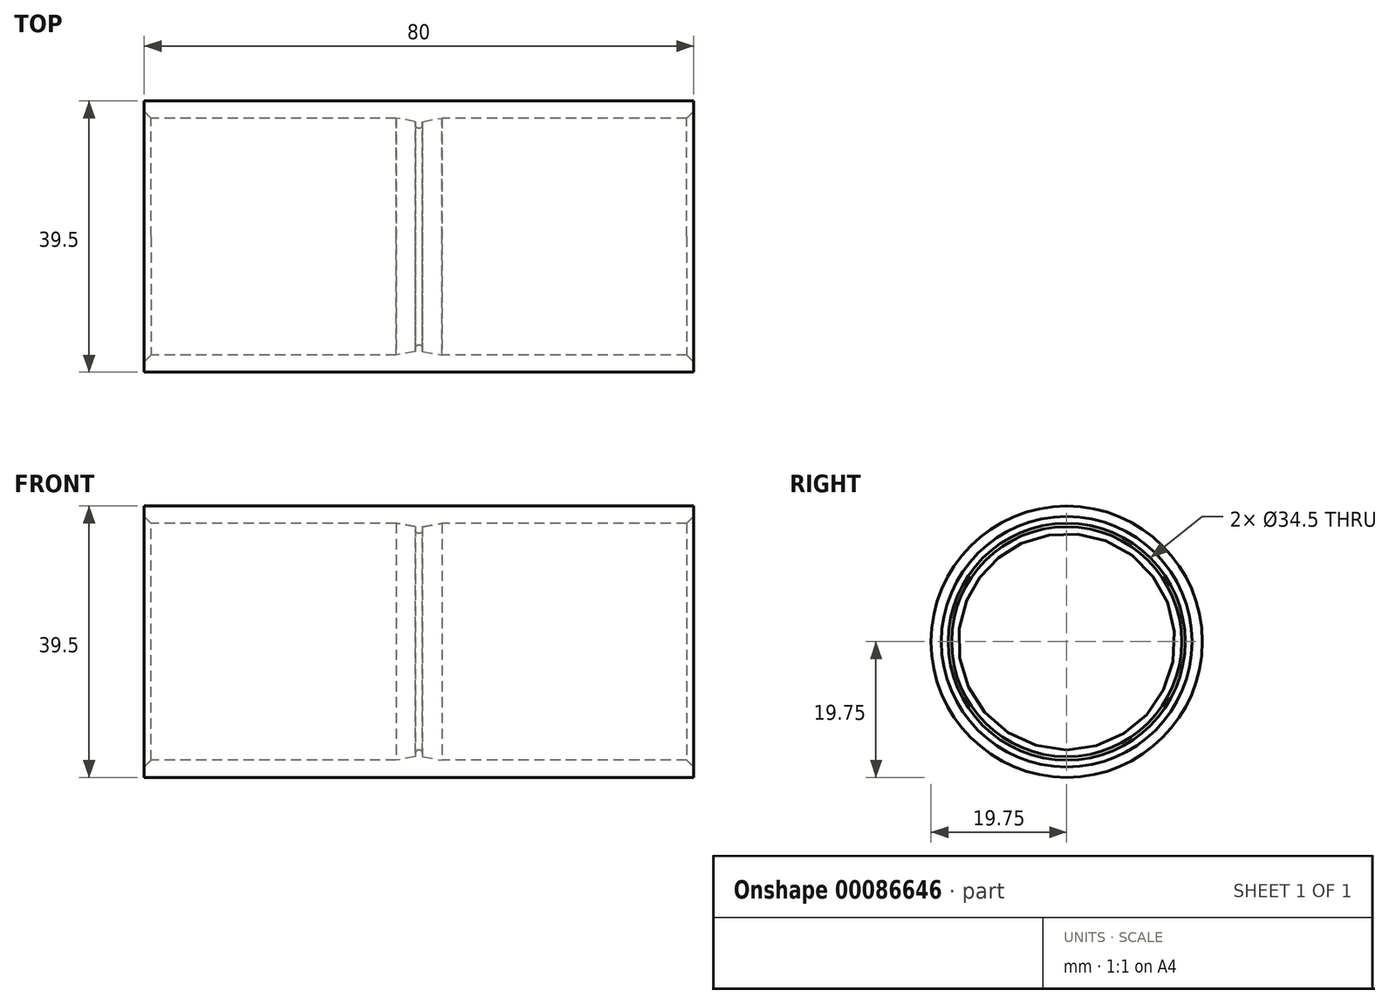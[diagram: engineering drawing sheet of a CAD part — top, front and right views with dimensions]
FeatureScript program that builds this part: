
annotation { "Feature Type Name" : "Feature", "Feature Type Description" : "" }
export const myFeature = defineFeature(function(context is Context, id is Id, definition is map)
    precondition{}
    {
        {
            var Q0;
            Q0=qCreatedBy(makeId("Top.planeOp"),FACE);
            var sketch = newSketch(context, id + "F0", { "sketchPlane" : qUnion([Q0])});
            skLineSegment(sketch, "E0", {"start": v(-40, 0) * mm, "end": v(40, 0) * mm, "construction": true});
            skLineSegment(sketch, "E1", {"start": v(-40, 19.75) * mm, "end": v(-40, 17.25) * mm});
            skLineSegment(sketch, "E2", {"start": v(-40, 17.25) * mm, "end": v(-3.34, 17.25) * mm});
            skLineSegment(sketch, "E3", {"start": v(-3.34, 17.25) * mm, "end": v(-0.5, 16.75) * mm});
            skLineSegment(sketch, "E4", {"start": v(-0.5, 16.75) * mm, "end": v(-0.5, 15.75) * mm});
            skLineSegment(sketch, "E5", {"start": v(0, 0) * mm, "end": v(0, 19.75) * mm, "construction": true});
            skLineSegment(sketch, "E6", {"start": v(-40, 19.75) * mm, "end": v(0, 19.75) * mm});
            skLineSegment(sketch, "E7", {"start": v(-0.5, 15.75) * mm, "end": v(0, 15.75) * mm});
            skLineSegment(sketch, "E8.MirrorCS", {"start": v(0.5, 15.75) * mm, "end": v(0, 15.75) * mm});
            skLineSegment(sketch, "E9.MirrorCS", {"start": v(0.5, 16.75) * mm, "end": v(0.5, 15.75) * mm});
            skLineSegment(sketch, "E10.MirrorCS", {"start": v(3.34, 17.25) * mm, "end": v(0.5, 16.75) * mm});
            skLineSegment(sketch, "E11.MirrorCS", {"start": v(40, 17.25) * mm, "end": v(3.34, 17.25) * mm});
            skLineSegment(sketch, "E12.MirrorCS", {"start": v(40, 19.75) * mm, "end": v(0, 19.75) * mm});
            skLineSegment(sketch, "E13.MirrorCS", {"start": v(40, 19.75) * mm, "end": v(40, 17.25) * mm});
            skSolve(sketch);
        }
        {
            var Q0;
            Q0=makeQuery(id+"F0.imprint","IMPRINT",FACE,{"disambiguationData":[TD([[makeQuery(id+"F0.imprint","IMPRINT",EDGE,{"derivedFrom":sQuery(id+"F0.wireOp",EDGE,"E1")}),1.0]])]});
            var Q1;
            Q1=sQuery(id+"F0.wireOp",EDGE,"E0");
            revolve(context, id + "F1", {"entities" : qUnion([Q0]), "axis" : qUnion([Q1]), "revolveType" : RevolveType.FULL});
        }
        {
            var Q0;
            Q0=makeQuery(id+"F1.opRevolve","SWEPT_EDGE",EDGE,{"disambiguationData":[OSD([sQuery(id+"F0.wireOp",EDGE,"E4"),sQuery(id+"F0.wireOp",EDGE,"E7")])]});
            var Q1;
            Q1=makeQuery(id+"F1.opRevolve","SWEPT_EDGE",EDGE,{"disambiguationData":[OSD([sQuery(id+"F0.wireOp",EDGE,"E8.MirrorCS"),sQuery(id+"F0.wireOp",EDGE,"E9.MirrorCS")])]});
            fillet(context, id + "F2", {"entities" : qUnion([Q0, Q1]), "radius" : 0.5 * mm, "tangentPropagation" : true, "allowEdgeOverflow" : false});
        }
        {
            var Q0;
            Q0=makeQuery(id+"F1.opRevolve","SWEPT_EDGE",EDGE,{"disambiguationData":[OSD([sQuery(id+"F0.wireOp",EDGE,"E1"),sQuery(id+"F0.wireOp",EDGE,"E2")])]});
            var Q1;
            Q1=makeQuery(id+"F1.opRevolve","SWEPT_EDGE",EDGE,{"disambiguationData":[OSD([sQuery(id+"F0.wireOp",EDGE,"E11.MirrorCS"),sQuery(id+"F0.wireOp",EDGE,"E13.MirrorCS")])]});
            chamfer(context, id + "F3", {"entities" : qUnion([Q0, Q1]), "width" : 1 * mm, "tangentPropagation" : true});
        }
    });
